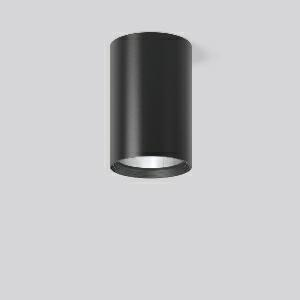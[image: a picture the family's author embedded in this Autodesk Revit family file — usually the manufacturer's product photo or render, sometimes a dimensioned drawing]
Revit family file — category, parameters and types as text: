
# Revit family: heledon_maxi_a_931218_003_3_53d2
name_source: partatom
category: Lighting Fixtures
units: mm (PartAtom-declared; Revit-internal decimal feet)

## family parameters
Cut with Voids When Loaded = No
Host = Face
Light Source = No
Part Type = Normal
Room Calculation Point = No
Round Connector Dimension = Use Diameter
Shared = No

## types (1)
- HELEDON maxi A (1 x LED Modul 935, 3400 lm, 3500)
    Apparent Load = 25 VA
    Approval mark = CE
    CIE Flux Codes = 100 100 100 100 100
    Color Rendering = 92
    Color Temperature = 3500
    Default Elevation = 1800 mm
    Description = Series: HELEDON maxi
Cylindrical surface-mounted downlight. Housing: die-cast aluminium, powder-coated. Internal ceiling frame polycarbonate with bayonet mounting. Black plastic ring and recessed LED to prevent glare from the side. Optical assembly with reflector made of MIRO-Silver with 98% total light reflection for outstanding efficiency - can be changed without tools. Best colour rendering index Ra>90. Suitable for Ceiling mounting. Easy installation with a separate ceiling frame with bayonet mounting and plug connection. Driver integrated. Connected via plug-in connector. High quality converter without flickering and stroboscopic effect. The following accessories can be mounted without use of tools: interchangeable lenses, decorative glasses, honeycomb louvre, clear and frosted diffusers, white interchangeable plastic ring. 
Colour: deep black, matt (RAL 9005)
Diameter: 123 mm
Height: 183 mm
Lamp: LED
Socket: without socket
Colour temperature: 3500K
Colour rendering index (CRI): 92
System power: 25 W
Rated luminous flux: 3400 lm
Luminous efficiency: 136 lm/W
Control gear: Regulated power supply
Protection class: I
Type of protection: IP 20
    Height = 183 mm
    Lamp = 1 x LED Modul 935
    Lamp Light Flux = 3400 lm
    Lamp count = 1
    Length = 123 mm
    Lifetime = 50000 h
    Luminous efficacy = 136 lm/W
    Manufacturer = RZB
    ModVariant = No
    Model = 931218.003.3
    Mounting Place = Ceiling
    Mounting Type = Surface mounted
    Number of Poles = 1
    OnlyDefault = Yes
    Power Factor = 1
    Product Name = HELEDON maxi A
    Product group = Surface mounted downlights
    ProductGroupID = 302
    Protection Class = Protection class I
    Protection Degree = IP 20
    RLX_Detail_Level = 1
    RLX_Emergency_Light_Flux = 0 lm
    RLX_Emergency_Type = 0
    RLX_Emergency_Type_DB = No
    RlxData = <blob elided: 96233 chars, md5=111cad17>
    Socket = socket
    Standby Power = 0 W
    System Light Flux = 3400 lm
    System Power = 25 W
    Type Comments = Product without accessories
    Type Image = 931192.003.jpg
    URL = http://relux.com
    VarID = ---
    Voltage = 230 V
    Voltage Range = 220-240 V
    Weight = 0.00 kg
    Width = 0 mm  [stored 0 ft]

note: [stored X ft] marks values corroborated as IEEE doubles in the binary element streams (Revit-internal decimal feet)

## geometry (parser evidence)
native form markers: Blend x4, Sweep x9
no freeform markers — native parametric forms only
